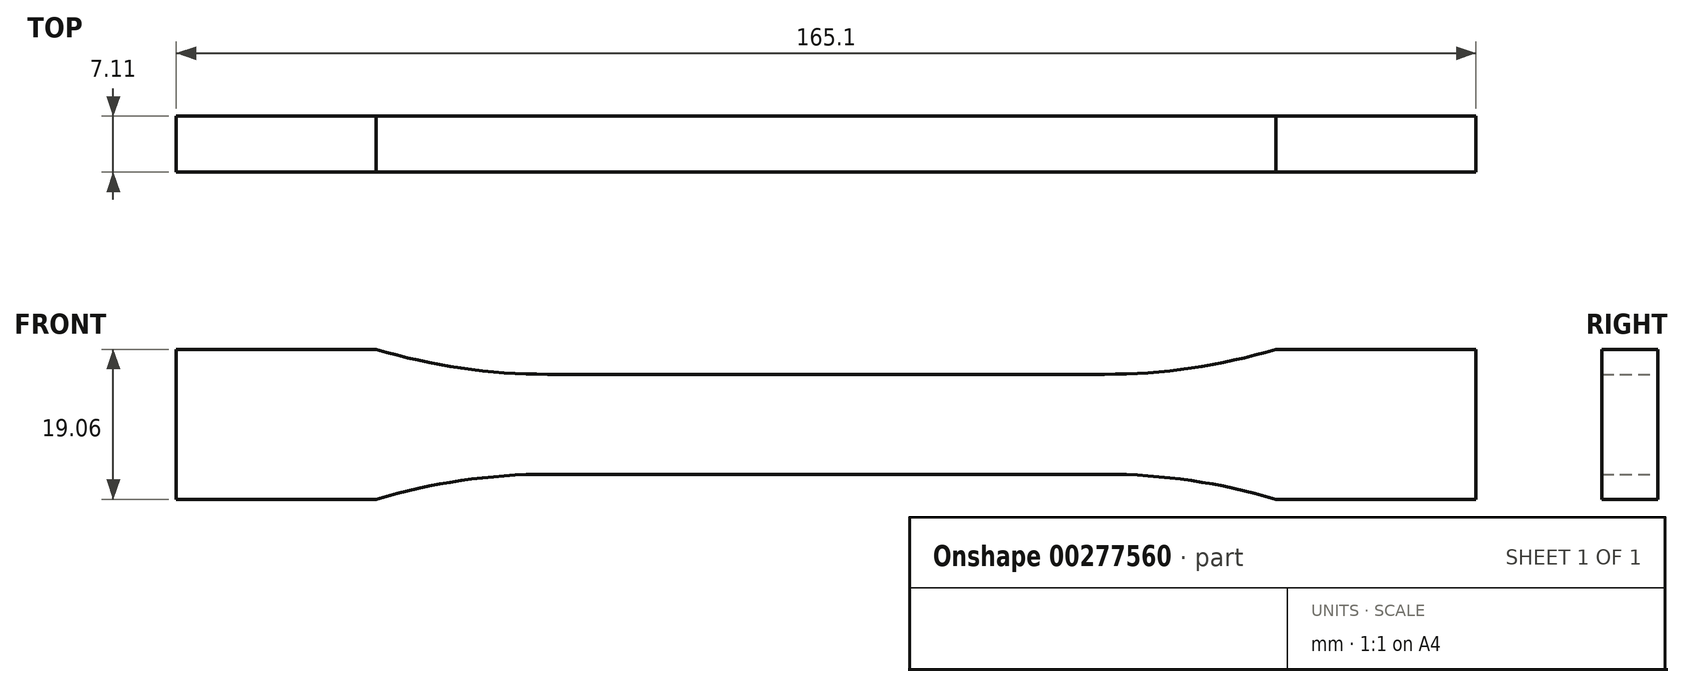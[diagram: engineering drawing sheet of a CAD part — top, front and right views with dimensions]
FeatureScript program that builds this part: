
annotation { "Feature Type Name" : "Feature", "Feature Type Description" : "" }
export const myFeature = defineFeature(function(context is Context, id is Id, definition is map)
    precondition{}
    {
        {
            var Q0;
            Q0=qCreatedBy(makeId("Front.planeOp"),FACE);
            var sketch = newSketch(context, id + "F0", { "sketchPlane" : qUnion([Q0])});
            skLineSegment(sketch, "E0", {"start": v(0, 6.35) * mm, "end": v(35.38, 6.35) * mm});
            skArc(sketch, "E1", {"start": v(35.38, 6.35) * mm, "mid": v(46.38, 7.15) * mm, "end": v(57.15, 9.52) * mm});
            skLineSegment(sketch, "E2", {"start": v(57.15, 9.53) * mm, "end": v(82.55, 9.53) * mm});
            skLineSegment(sketch, "E3.MirrorCS", {"start": v(57.15, -9.53) * mm, "end": v(82.55, -9.53) * mm});
            skLineSegment(sketch, "E4.MirrorCS", {"start": v(0, -6.35) * mm, "end": v(35.38, -6.35) * mm});
            skArc(sketch, "E5.MirrorCS", {"start": v(35.38, -6.35) * mm, "mid": v(46.38, -7.15) * mm, "end": v(57.15, -9.52) * mm});
            skLineSegment(sketch, "E6.MirrorCS", {"start": v(-57.15, -9.53) * mm, "end": v(-82.55, -9.53) * mm});
            skArc(sketch, "E7.MirrorCS", {"start": v(-35.38, 6.35) * mm, "mid": v(-46.38, 7.15) * mm, "end": v(-57.15, 9.52) * mm});
            skLineSegment(sketch, "E8.MirrorCS", {"start": v(0, 6.35) * mm, "end": v(-35.38, 6.35) * mm});
            skLineSegment(sketch, "E9.MirrorCS", {"start": v(-57.15, 9.52) * mm, "end": v(-82.55, 9.52) * mm});
            skLineSegment(sketch, "E10.MirrorCS", {"start": v(0, -6.35) * mm, "end": v(-35.38, -6.35) * mm});
            skArc(sketch, "E11.MirrorCS", {"start": v(-35.38, -6.35) * mm, "mid": v(-46.38, -7.15) * mm, "end": v(-57.15, -9.52) * mm});
            skLineSegment(sketch, "E12", {"start": v(-82.55, 9.53) * mm, "end": v(-82.55, -9.53) * mm});
            skLineSegment(sketch, "E13", {"start": v(82.55, 9.53) * mm, "end": v(82.55, -9.53) * mm});
            skSolve(sketch);
        }
        {
            var Q0;
            Q0 = qSketchRegion(id + "F0", true);
            extrude(context, id + "F1", {"entities" : qUnion([Q0]), "depth" : 7.11 * mm});
        }
    });
